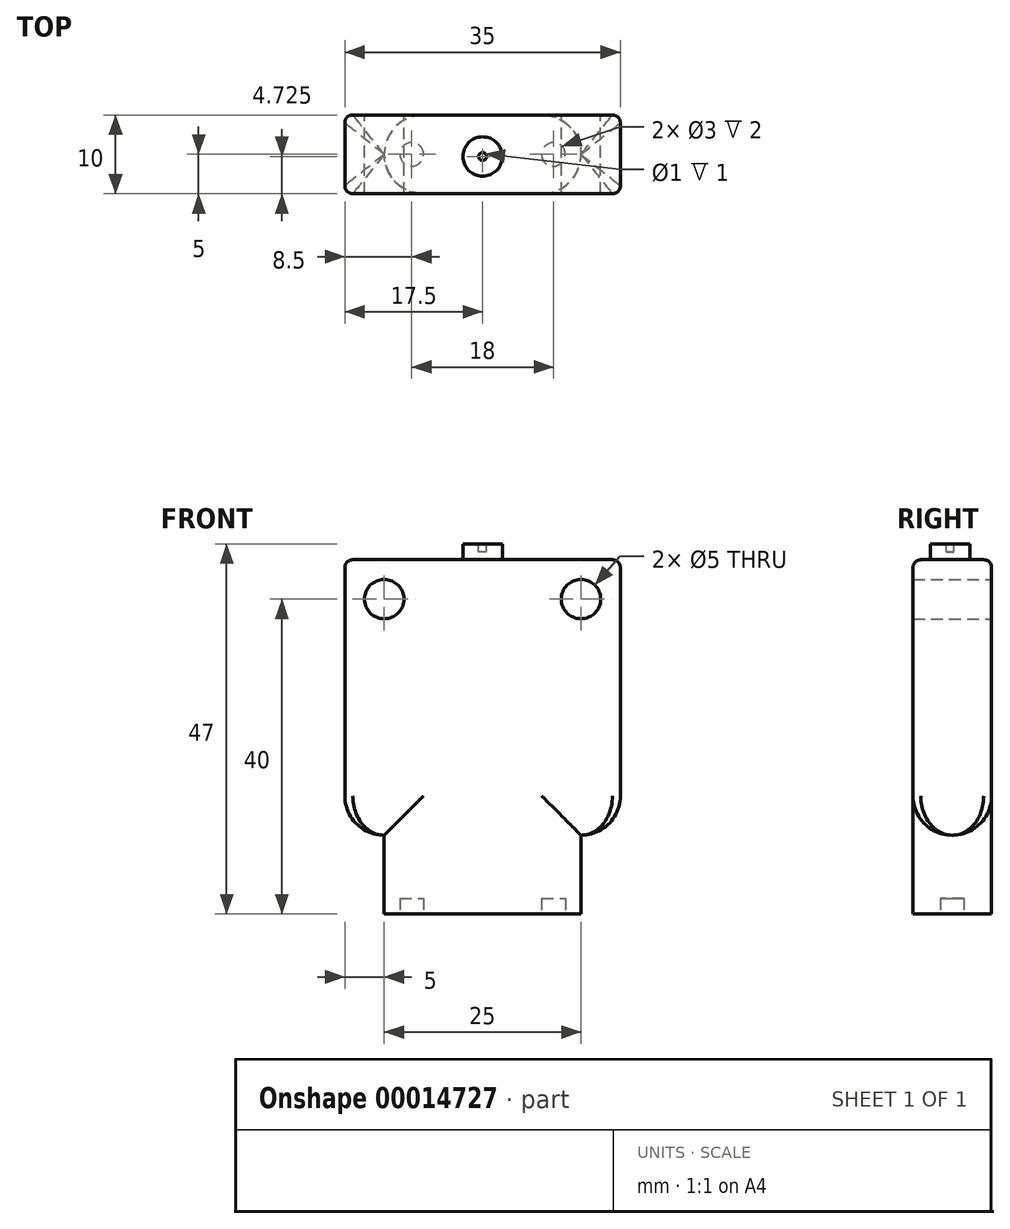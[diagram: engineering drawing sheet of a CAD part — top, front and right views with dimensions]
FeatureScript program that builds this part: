
annotation { "Feature Type Name" : "Feature", "Feature Type Description" : "" }
export const myFeature = defineFeature(function(context is Context, id is Id, definition is map)
    precondition{}
    {
        {
            var Q0;
            Q0=qCreatedBy(makeId("Top.planeOp"),FACE);
            var sketch = newSketch(context, id + "F0", { "sketchPlane" : qUnion([Q0])});
            skLineSegment(sketch, "E0.bottom", {"start": v(0, 0) * mm, "end": v(-25, 0) * mm});
            skLineSegment(sketch, "E0.top", {"start": v(0, 10) * mm, "end": v(-25, 10) * mm});
            skLineSegment(sketch, "E0.left", {"start": v(0, 0) * mm, "end": v(0, 10) * mm});
            skLineSegment(sketch, "E0.right", {"start": v(-25, 0) * mm, "end": v(-25, 10) * mm});
            skSolve(sketch);
        }
        {
            var Q0;
            Q0=qSketchRegion(id+"F0",true);
            extrude(context, id + "F1", {"entities" : qUnion([Q0]), "depth" : 10 * mm});
        }
        {
            var Q0;
            Q0=makeQuery(id+"F1.opExtrude","CAP_FACE",FACE,{"disambiguationData":[OSD([sQuery(id+"F0.wireOp",EDGE,"E0.bottom"),sQuery(id+"F0.wireOp",EDGE,"E0.top"),sQuery(id+"F0.wireOp",EDGE,"E0.left"),sQuery(id+"F0.wireOp",EDGE,"E0.right")])],"isStart":true});
            var sketch = newSketch(context, id + "F2", { "sketchPlane" : qUnion([Q0])});
            skCircle(sketch, "E1", {"center": v(-21.5, -5) * mm, "radius": 1.5 * mm});
            skCircle(sketch, "E2", {"center": v(-3.5, -5) * mm, "radius": 1.5 * mm});
            skSolve(sketch);
        }
        {
            var Q0;
            Q0=qSketchRegion(id+"F2",true);
            extrude(context, id + "F3", {"entities" : qUnion([Q0]), "operationType" : NewBodyOperationType.REMOVE, "oppositeDirection" : true, "depth" : 2 * mm});
        }
        {
            var Q0;
            Q0=makeQuery(id+"F1.opExtrude","SWEPT_EDGE",EDGE,{"disambiguationData":[OSD([sQuery(id+"F0.wireOp",EDGE,"E0.bottom"),sQuery(id+"F0.wireOp",EDGE,"E0.right")])]});
            var Q1;
            Q1=makeQuery(id+"F1.opExtrude","SWEPT_EDGE",EDGE,{"disambiguationData":[OSD([sQuery(id+"F0.wireOp",EDGE,"E0.top"),sQuery(id+"F0.wireOp",EDGE,"E0.right")])]});
            var Q2;
            Q2=makeQuery(id+"F1.opExtrude","SWEPT_EDGE",EDGE,{"disambiguationData":[OSD([sQuery(id+"F0.wireOp",EDGE,"E0.bottom"),sQuery(id+"F0.wireOp",EDGE,"E0.left")])]});
            var Q3;
            Q3=makeQuery(id+"F1.opExtrude","SWEPT_EDGE",EDGE,{"disambiguationData":[OSD([sQuery(id+"F0.wireOp",EDGE,"E0.top"),sQuery(id+"F0.wireOp",EDGE,"E0.left")])]});
            fillet(context, id + "F4", {"entities" : qUnion([Q0, Q1, Q2, Q3]), "radius" : 5 * mm, "tangentPropagation" : true, "allowEdgeOverflow" : false});
        }
        {
            var Q0;
            Q0=qCreatedBy(makeId("Front.planeOp"),FACE);
            var sketch = newSketch(context, id + "F5", { "sketchPlane" : qUnion([Q0])});
            skLineSegment(sketch, "E3.bottom", {"start": v(5, 10) * mm, "end": v(-30, 10) * mm});
            skLineSegment(sketch, "E3.top", {"start": v(5, 45) * mm, "end": v(-30, 45) * mm});
            skLineSegment(sketch, "E3.left", {"start": v(5, 10) * mm, "end": v(5, 45) * mm});
            skLineSegment(sketch, "E3.right", {"start": v(-30, 10) * mm, "end": v(-30, 45) * mm});
            skSolve(sketch);
        }
        {
            var Q0;
            Q0=qSketchRegion(id+"F5",true);
            extrude(context, id + "F6", {"entities" : qUnion([Q0]), "operationType" : NewBodyOperationType.ADD, "oppositeDirection" : true, "depth" : 10 * mm});
        }
        {
            var Q0;
            {var subQ0=sQuery(id+"F5.wireOp",EDGE,"E3.bottom");var subQ1=sQuery(id+"F5.wireOp",EDGE,"E3.left");Q0=makeQuery(id+"F6.boolean.opBoolean","SPLIT",EDGE,{"disambiguationData":[TD([makeQuery(id+"F6.opExtrude","SWEPT_FACE",FACE,{"disambiguationData":[OSD([subQ1])]})])],"derivedFrom":makeQuery(id+"F6.opExtrude","CAP_EDGE",EDGE,{"disambiguationData":[OSD([subQ0])],"isStart":false})});}
            var Q1;
            {var subQ0=sQuery(id+"F5.wireOp",EDGE,"E3.bottom");var subQ1=sQuery(id+"F5.wireOp",EDGE,"E3.left");Q1=makeQuery(id+"F6.boolean.opBoolean","SPLIT",EDGE,{"disambiguationData":[TD([makeQuery(id+"F6.opExtrude","SWEPT_FACE",FACE,{"disambiguationData":[OSD([subQ1])]})])],"derivedFrom":makeQuery(id+"F6.opExtrude","CAP_EDGE",EDGE,{"disambiguationData":[OSD([subQ0])],"isStart":true})});}
            var Q2;
            {var subQ0=sQuery(id+"F5.wireOp",EDGE,"E3.bottom");var subQ1=sQuery(id+"F5.wireOp",EDGE,"E3.right");Q2=makeQuery(id+"F6.boolean.opBoolean","SPLIT",EDGE,{"disambiguationData":[TD([makeQuery(id+"F6.opExtrude","SWEPT_FACE",FACE,{"disambiguationData":[OSD([subQ1])]})])],"derivedFrom":makeQuery(id+"F6.opExtrude","CAP_EDGE",EDGE,{"disambiguationData":[OSD([subQ0])],"isStart":false})});}
            var Q3;
            {var subQ0=sQuery(id+"F5.wireOp",EDGE,"E3.bottom");var subQ1=sQuery(id+"F5.wireOp",EDGE,"E3.right");Q3=makeQuery(id+"F6.boolean.opBoolean","SPLIT",EDGE,{"disambiguationData":[TD([makeQuery(id+"F6.opExtrude","SWEPT_FACE",FACE,{"disambiguationData":[OSD([subQ1])]})])],"derivedFrom":makeQuery(id+"F6.opExtrude","CAP_EDGE",EDGE,{"disambiguationData":[OSD([subQ0])],"isStart":true})});}
            var Q4;
            Q4=makeQuery(id+"F6.opExtrude","SWEPT_EDGE",EDGE,{"disambiguationData":[OSD([sQuery(id+"F5.wireOp",EDGE,"E3.bottom"),sQuery(id+"F5.wireOp",EDGE,"E3.left")])]});
            var Q5;
            Q5=makeQuery(id+"F6.opExtrude","SWEPT_EDGE",EDGE,{"disambiguationData":[OSD([sQuery(id+"F5.wireOp",EDGE,"E3.bottom"),sQuery(id+"F5.wireOp",EDGE,"E3.right")])]});
            fillet(context, id + "F7", {"entities" : qUnion([Q0, Q1, Q2, Q3, Q4, Q5]), "radius" : 5 * mm, "tangentPropagation" : true, "allowEdgeOverflow" : false});
        }
        {
            var Q0;
            Q0=makeQuery(id+"F6.boolean.opBoolean","MERGE",FACE,{"derivedFrom":[makeQuery(id+"F1.opExtrude","SWEPT_FACE",FACE,{"disambiguationData":[OSD([sQuery(id+"F0.wireOp",EDGE,"E0.top")])]}),makeQuery(id+"F6.opExtrude","CAP_FACE",FACE,{"disambiguationData":[OSD([sQuery(id+"F5.wireOp",EDGE,"E3.bottom"),sQuery(id+"F5.wireOp",EDGE,"E3.top"),sQuery(id+"F5.wireOp",EDGE,"E3.left"),sQuery(id+"F5.wireOp",EDGE,"E3.right")])],"isStart":false})]});
            var sketch = newSketch(context, id + "F8", { "sketchPlane" : qUnion([Q0])});
            skCircle(sketch, "E4", {"center": v(0, 40) * mm, "radius": 2.5 * mm});
            skCircle(sketch, "E5", {"center": v(25, 40) * mm, "radius": 2.5 * mm});
            skSolve(sketch);
        }
        {
            var Q0;
            Q0=qSketchRegion(id+"F8",true);
            extrude(context, id + "F9", {"entities" : qUnion([Q0]), "operationType" : NewBodyOperationType.REMOVE, "endBound" : BoundingType.THROUGH_ALL, "oppositeDirection" : true, "depth" : 25 * mm});
        }
        {
            var Q0;
            Q0=makeQuery(id+"F6.opExtrude","SWEPT_FACE",FACE,{"disambiguationData":[OSD([sQuery(id+"F5.wireOp",EDGE,"E3.top")])]});
            var sketch = newSketch(context, id + "F10", { "sketchPlane" : qUnion([Q0])});
            skCircle(sketch, "E6", {"center": v(-12.5, 4.73) * mm, "radius": 2.5 * mm});
            skSolve(sketch);
        }
        {
            var Q0;
            Q0=qSketchRegion(id+"F10",true);
            extrude(context, id + "F11", {"entities" : qUnion([Q0]), "operationType" : NewBodyOperationType.ADD, "depth" : 2 * mm});
        }
        {
            var Q0;
            Q0=makeQuery(id+"F11.opExtrude","CAP_FACE",FACE,{"disambiguationData":[OSD([sQuery(id+"F10.wireOp",EDGE,"E6")])],"isStart":false});
            var sketch = newSketch(context, id + "F12", { "sketchPlane" : qUnion([Q0])});
            skCircle(sketch, "E7", {"center": v(-12.5, 4.73) * mm, "radius": 0.5 * mm});
            skSolve(sketch);
        }
        {
            var Q0;
            Q0=qSketchRegion(id+"F12",true);
            extrude(context, id + "F13", {"entities" : qUnion([Q0]), "operationType" : NewBodyOperationType.REMOVE, "oppositeDirection" : true, "depth" : 1 * mm});
        }
        {
            var Q0;
            Q0=makeQuery(id+"F6.opExtrude","CAP_EDGE",EDGE,{"disambiguationData":[OSD([sQuery(id+"F5.wireOp",EDGE,"E3.top")])],"isStart":true});
            var Q1;
            Q1=makeQuery(id+"F6.opExtrude","CAP_EDGE",EDGE,{"disambiguationData":[OSD([sQuery(id+"F5.wireOp",EDGE,"E3.top")])],"isStart":false});
            var Q2;
            Q2=makeQuery(id+"F6.opExtrude","SWEPT_EDGE",EDGE,{"disambiguationData":[OSD([sQuery(id+"F5.wireOp",EDGE,"E3.top"),sQuery(id+"F5.wireOp",EDGE,"E3.left")])]});
            var Q3;
            Q3=makeQuery(id+"F6.opExtrude","SWEPT_EDGE",EDGE,{"disambiguationData":[OSD([sQuery(id+"F5.wireOp",EDGE,"E3.top"),sQuery(id+"F5.wireOp",EDGE,"E3.right")])]});
            var Q4;
            Q4=makeQuery(id+"F6.opExtrude","CAP_EDGE",EDGE,{"disambiguationData":[OSD([sQuery(id+"F5.wireOp",EDGE,"E3.left")])],"isStart":true});
            var Q5;
            Q5=makeQuery(id+"F6.opExtrude","CAP_EDGE",EDGE,{"disambiguationData":[OSD([sQuery(id+"F5.wireOp",EDGE,"E3.left")])],"isStart":false});
            var Q6;
            Q6=makeQuery(id+"F6.opExtrude","CAP_EDGE",EDGE,{"disambiguationData":[OSD([sQuery(id+"F5.wireOp",EDGE,"E3.right")])],"isStart":false});
            var Q7;
            Q7=makeQuery(id+"F6.opExtrude","CAP_EDGE",EDGE,{"disambiguationData":[OSD([sQuery(id+"F5.wireOp",EDGE,"E3.right")])],"isStart":true});
            fillet(context, id + "F14", {"entities" : qUnion([Q0, Q1, Q2, Q3, Q4, Q5, Q6, Q7]), "radius" : 1 * mm, "tangentPropagation" : true, "allowEdgeOverflow" : false});
        }
    });
